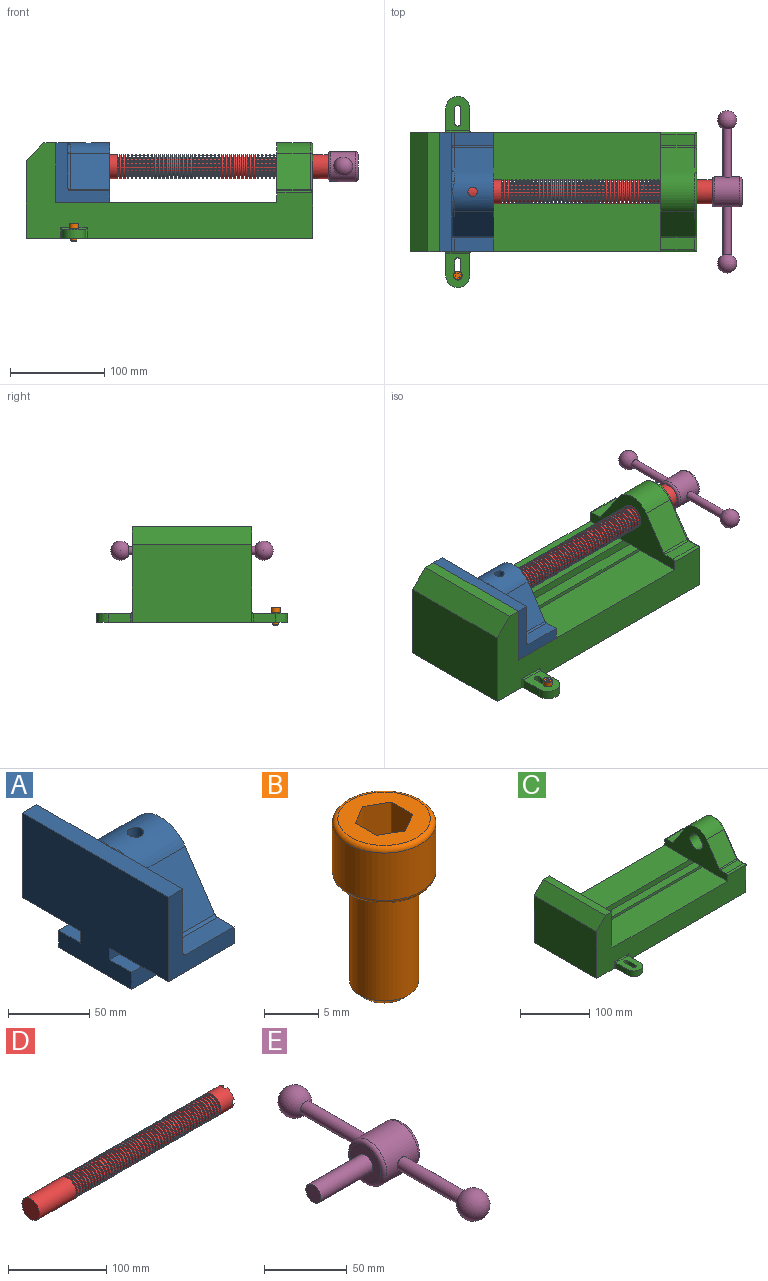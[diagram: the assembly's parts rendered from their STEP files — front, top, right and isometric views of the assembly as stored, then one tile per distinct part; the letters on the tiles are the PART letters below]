
ASSEMBLY  parts=5 mates=5
PART A: 36 faces, bbox 57.2x127x89 mm
  f0: plane 57.15x50.8mm, normal (0,0,-1), area 2903.2mm2, adj f6,f9,f10,f23
  f1: cylinder r=12.7mm len=44.45mm, axis (1,0,0), area 3464.3mm2, adj f6,f15,f16
  f2: plane 41.91x14.52mm, normal (0,0,1), area 608.5mm2, adj f6,f11,f24,f25
  f3: plane 51.86x48.26mm, normal (1,0,0), area 1495.7mm2, adj f8,f10,f31,f33,f35
  f4: plane 51.86x48.26mm, normal (1,0,0), area 1495.7mm2, adj f8,f11,f24,f28,f29
  f5: plane 57.15x50.8mm, normal (0,0,-1), area 2903.2mm2, adj f6,f9,f11,f22
  f6: plane 127x85.09mm, normal (1,0,0), area 5190.6mm2, adj f0,f1,f2,f5,f7,f10,f11,f12
  f7: plane 41.91x14.52mm, normal (0,0,1), area 608.5mm2, adj f6,f10,f30,f31
  f8: plane 127x12.7mm, normal (0,0,1), area 1612.9mm2, adj f3,f4,f9,f10,f11,f26,f34
  f9: plane 127x85.09mm, normal (-1,0,0), area 9096.8mm2, adj f0,f5,f8,f10,f11,f17,f18,f19
  f10: plane 63.5x57.15mm, normal (0,-1,0), area 1372.3mm2, adj f0,f3,f6,f7,f8,f9,f31
  f11: plane 63.5x57.15mm, normal (0,1,0), area 1372.3mm2, adj f2,f4,f5,f6,f8,f9,f24
  f12: plane 41.91x38.43mm, normal (0,-0.83,0.56), area 1939.2mm2, adj f6,f13,f30,f33
  f13: cylinder r=25.4mm len=44.45mm, axis (1,0,0), area 2026.5mm2, adj f6,f12,f14,f16,f26,f28,f34,f35
  f14: plane 41.91x38.43mm, normal (0,0.83,0.56), area 1939.2mm2, adj f6,f13,f25,f29
  f15: plane 25.4x25.4mm, normal (1,0,0), area 506.7mm2, adj f1
  f16: cylinder r=5.08mm len=13.76mm, axis (0,0,1), area 414mm2, adj f1,f13
  f17: plane 57.15x19.05mm, normal (0,0,1), area 1088.7mm2, adj f6,f9,f18,f23
  f18: plane 57.15x12.7mm, normal (0,-1,0), area 725.8mm2, adj f6,f9,f17,f19
  f19: plane 63.5x57.15mm, normal (0,0,-1), area 3629mm2, adj f6,f9,f18,f20
  f20: plane 57.15x12.7mm, normal (0,1,0), area 725.8mm2, adj f6,f9,f19,f21
  f21: plane 57.15x19.05mm, normal (0,0,1), area 1088.7mm2, adj f6,f9,f20,f22
  f22: plane 57.15x8.89mm, normal (0,1,0), area 508.1mm2, adj f5,f6,f9,f21
  f23: plane 57.15x8.89mm, normal (0,-1,0), area 508.1mm2, adj f0,f6,f9,f17
  f24: cylinder r=2.54mm len=14.52mm, axis (0,-1,0), area 57.9mm2, adj f2,f4,f11,f27
  f25: cylinder r=2.54mm len=41.91mm, axis (1,0,0), area 104.3mm2, adj f2,f6,f14,f27
  f26: bspline ~12.24x2.8mm, area 20.9mm2, adj f8,f13,f28
  f27: sphere r=2.54mm, area 6.3mm2, adj f24,f25,f29
  f28: torus R=27.94mm, axis (1,0,0), area 57.8mm2, adj f4,f13,f26,f29
  f29: cylinder r=2.54mm len=39.84mm, axis (0,-0.56,0.83), area 184.6mm2, adj f4,f14,f27,f28
  f30: cylinder r=2.54mm len=41.91mm, axis (1,0,0), area 104.3mm2, adj f6,f7,f12,f32
  f31: cylinder r=2.54mm len=14.52mm, axis (0,-1,0), area 57.9mm2, adj f3,f7,f10,f32
  f32: sphere r=2.54mm, area 6.3mm2, adj f30,f31,f33
  f33: cylinder r=2.54mm len=39.84mm, axis (0,-0.56,-0.83), area 184.6mm2, adj f3,f12,f32,f35
  f34: bspline ~12.24x2.8mm, area 20.9mm2, adj f8,f13,f35
  f35: torus R=27.94mm, axis (1,0,0), area 57.8mm2, adj f3,f13,f33,f34
PART B: 15 faces, bbox 10.3x10.3x19.1 mm
  f0: plane 8.51x8.51mm, normal (0,0,1), area 37.2mm2, adj f5,f6,f7,f8,f9,f10,f14
  f1: cylinder r=3.17mm len=11.94mm, axis (0,0,1), area 238.2mm2, adj f4,f12
  f2: plane 4.83x4.83mm, normal (0,0,-1), area 18.3mm2, adj f12
  f3: cylinder r=4.76mm len=9.53mm, axis (0,0,-1), area 159.6mm2, adj f13,f14
  f4: plane 8.51x8.51mm, normal (0,0,-1), area 25.2mm2, adj f1,f13
  f5: plane 4.83x2.38mm, normal (-0.5,-0.87,0), area 13.3mm2, adj f0,f6,f10,f11
  f6: plane 4.83x2.38mm, normal (0.5,-0.87,0), area 13.3mm2, adj f0,f5,f7,f11
  f7: plane 4.83x2.75mm, normal (1,0,0), area 13.3mm2, adj f0,f6,f8,f11
  f8: plane 4.83x2.38mm, normal (0.5,0.87,0), area 13.3mm2, adj f0,f7,f9,f11
  f9: plane 4.83x2.38mm, normal (-0.5,0.87,0), area 13.3mm2, adj f0,f8,f10,f11
  f10: plane 4.83x2.75mm, normal (-1,0,0), area 13.3mm2, adj f0,f5,f9,f11
  f11: plane 5.5x4.76mm, normal (0,0,1), area 19.6mm2, adj f5,f6,f7,f8,f9,f10
  f12: cone r=3.17mm half-angle=45deg, axis (0,0,1), area 18.9mm2, adj f1,f2
  f13: torus R=4.25mm, axis (0,0,1), area 23mm2, adj f3,f4
  f14: torus R=4.25mm, axis (0,0,1), area 23mm2, adj f0,f3
PART C: 61 faces, bbox 304.8x203.2x103.7 mm
  f0: plane 304.8x101.6mm, normal (0,1,0), area 13520.3mm2, adj f3,f4,f5,f6,f7,f8,f9,f16
  f1: plane 304.8x101.6mm, normal (0,-1,0), area 13520.3mm2, adj f2,f3,f5,f6,f7,f8,f9,f16
  f2: plane 234.95x50.8mm, normal (0,0,1), area 11935.5mm2, adj f1,f5,f16,f26
  f3: plane 127x99.06mm, normal (1,0,0), area 7097.5mm2, adj f0,f1,f9,f14,f17,f18,f19,f20
  f4: plane 234.95x50.8mm, normal (0,0,1), area 11935.5mm2, adj f0,f5,f16,f27
  f5: plane 127x101.6mm, normal (1,0,0), area 9516.1mm2, adj f0,f1,f2,f4,f6,f9,f18,f19
  f6: plane 127x12.7mm, normal (0,0,1), area 1612.9mm2, adj f0,f1,f5,f7
  f7: plane 127x19.05mm, normal (-0.71,0,0.71), area 3421.5mm2, adj f0,f1,f6,f8
  f8: plane 127x82.55mm, normal (-1,0,0), area 10483.8mm2, adj f0,f1,f7,f9
  f9: plane 304.8x203.2mm, normal (0,0,-1), area 33298.3mm2, adj f0,f1,f3,f5,f8,f21,f22,f39
  f10: plane 35.56x11.98mm, normal (0,0,1), area 426mm2, adj f16,f28,f29,f30
  f11: plane 38.43x35.56mm, normal (0,0.83,0.56), area 1645.4mm2, adj f12,f16,f29,f32
  f12: cylinder r=25.4mm len=42.19mm, axis (1,0,0), area 1770.2mm2, adj f11,f13,f16,f33
  f13: plane 38.43x35.56mm, normal (0,-0.83,0.56), area 1645.4mm2, adj f12,f16,f34,f35
  f14: cylinder r=12.7mm len=38.1mm, axis (1,0,0), area 3040.2mm2, adj f3,f16
  f15: plane 35.56x11.98mm, normal (0,0,1), area 426mm2, adj f16,f34,f36,f38
  f16: plane 127x63.5mm, normal (-1,0,0), area 4155.5mm2, adj f0,f1,f2,f4,f10,f11,f12,f13
  f17: plane 38.1x25.4mm, normal (0,0,-1), area 967.7mm2, adj f3,f16,f26,f27
  f18: plane 273.05x19.05mm, normal (0,0,-1), area 5201.6mm2, adj f3,f5,f19,f26
  f19: plane 273.05x12.7mm, normal (0,1,0), area 3467.7mm2, adj f3,f5,f18,f20
  f20: plane 273.05x19.05mm, normal (0,0,1), area 5201.6mm2, adj f3,f5,f19,f21
  f21: plane 273.05x16.51mm, normal (0,1,0), area 4508.1mm2, adj f3,f5,f9,f20
  f22: plane 273.05x16.51mm, normal (0,-1,0), area 4508.1mm2, adj f3,f5,f9,f23
  f23: plane 273.05x19.05mm, normal (0,0,1), area 5201.6mm2, adj f3,f5,f22,f24
  f24: plane 273.05x12.7mm, normal (0,-1,0), area 3467.7mm2, adj f3,f5,f23,f25
  f25: plane 273.05x19.05mm, normal (0,0,-1), area 5201.6mm2, adj f3,f5,f24,f27
  f26: plane 273.05x8.89mm, normal (0,1,0), area 2427.4mm2, adj f2,f3,f5,f17,f18
  f27: plane 273.05x8.89mm, normal (0,-1,0), area 2427.4mm2, adj f3,f4,f5,f17,f25
  f28: cylinder r=2.54mm len=38.1mm, axis (1,0,0), area 148.3mm2, adj f0,f10,f16,f30
  f29: cylinder r=2.54mm len=35.56mm, axis (-1,0,0), area 88.5mm2, adj f10,f11,f16,f31
  f30: cylinder r=2.54mm len=14.52mm, axis (0,1,0), area 54.3mm2, adj f3,f10,f28,f31
  f31: torus R=5.08mm, axis (-1,0,0), area 13.5mm2, adj f3,f29,f30,f32
  f32: cylinder r=2.54mm len=39.84mm, axis (0,0.56,-0.83), area 184.6mm2, adj f3,f11,f31,f33
  f33: torus R=22.86mm, axis (-1,0,0), area 191.4mm2, adj f3,f12,f32,f35
  f34: cylinder r=2.54mm len=35.56mm, axis (-1,0,0), area 88.5mm2, adj f13,f15,f16,f37
  f35: cylinder r=2.54mm len=39.84mm, axis (0,0.56,0.83), area 184.6mm2, adj f3,f13,f33,f37
  f36: cylinder r=2.54mm len=38.1mm, axis (-1,0,0), area 148.3mm2, adj f1,f15,f16,f38
  f37: torus R=5.08mm, axis (-1,0,0), area 13.5mm2, adj f3,f34,f35,f38
  f38: cylinder r=2.54mm len=14.52mm, axis (0,1,0), area 54.3mm2, adj f3,f15,f36,f37
  f39: plane 23.88x9.53mm, normal (-1,0,0), area 227.4mm2, adj f9,f45,f46,f60
  f40: plane 23.88x9.53mm, normal (1,0,0), area 227.4mm2, adj f9,f45,f46,f58
  f41: cylinder r=3.3mm len=9.53mm, axis (0,0,-1), area 98.8mm2, adj f9,f42,f44,f46
  f42: plane 15.62x9.53mm, normal (-1,0,0), area 148.8mm2, adj f9,f41,f43,f46
  f43: cylinder r=3.3mm len=9.53mm, axis (0,0,-1), area 98.8mm2, adj f9,f42,f44,f46
  f44: plane 15.62x9.53mm, normal (1,0,0), area 148.8mm2, adj f9,f41,f43,f46
  f45: cylinder r=12.7mm len=25.4mm, axis (0,0,-1), area 380mm2, adj f9,f39,f40,f46
  f46: plane 36.58x25.4mm, normal (0,0,1), area 722.4mm2, adj f39,f40,f41,f42,f43,f44,f45,f59
  f47: plane 23.88x9.53mm, normal (-1,0,0), area 227.4mm2, adj f9,f53,f54,f56
  f48: plane 23.88x9.53mm, normal (1,0,0), area 227.4mm2, adj f9,f53,f54,f55
  f49: cylinder r=3.3mm len=9.53mm, axis (0,0,-1), area 98.8mm2, adj f9,f50,f52,f54
  f50: plane 15.62x9.53mm, normal (-1,0,0), area 148.8mm2, adj f9,f49,f51,f54
  f51: cylinder r=3.3mm len=9.53mm, axis (0,0,-1), area 98.8mm2, adj f9,f50,f52,f54
  f52: plane 15.62x9.53mm, normal (1,0,0), area 148.8mm2, adj f9,f49,f51,f54
  f53: cylinder r=12.7mm len=25.4mm, axis (0,0,-1), area 380mm2, adj f9,f47,f48,f54
  f54: plane 36.58x25.4mm, normal (0,0,1), area 722.4mm2, adj f47,f48,f49,f50,f51,f52,f53,f57
  f55: cylinder r=1.52mm len=11.05mm, axis (0,0,-1), area 24.1mm2, adj f0,f9,f48,f57
  f56: cylinder r=1.52mm len=11.05mm, axis (0,0,1), area 24.1mm2, adj f0,f9,f47,f57
  f57: cylinder r=1.52mm len=28.45mm, axis (1,0,0), area 63.5mm2, adj f0,f54,f55,f56
  f58: cylinder r=1.52mm len=11.05mm, axis (0,0,1), area 24.1mm2, adj f1,f9,f40,f59
  f59: cylinder r=1.52mm len=28.45mm, axis (-1,0,0), area 63.5mm2, adj f1,f46,f58,f60
  f60: cylinder r=1.52mm len=11.05mm, axis (0,0,-1), area 24.1mm2, adj f1,f9,f39,f59
PART D: 220 faces, bbox 279.4x25.4x25.4 mm
  f0: cylinder r=12.7mm len=25.4mm, axis (-1,0,0), area 1468.2mm2, adj f1,f2,f3,f5,f7,f208,f209,f210
  f1: plane 9.9x9.9mm, normal (1,0,0), area 62.3mm2, adj f0,f4,f213,f216
  f2: plane 9.9x9.9mm, normal (1,0,0), area 62.3mm2, adj f0,f4,f210,f218
  f3: plane 9.9x9.9mm, normal (1,0,0), area 62.3mm2, adj f0,f4,f209,f212
  f4: cylinder r=6.35mm len=25.4mm, axis (1,0,0), area 960.3mm2, adj f1,f2,f3,f5,f6,f208,f209,f210
  f5: plane 9.9x9.9mm, normal (1,0,0), area 62.3mm2, adj f0,f4,f215,f217
  f6: plane 12.7x12.7mm, normal (1,0,0), area 126.7mm2, adj f4
  f7: cone r=12.7mm half-angle=76deg, axis (1,0,0), area 188mm2, adj f0,f9
  f8: cone r=10.16mm half-angle=76deg, axis (-1,0,0), area 188mm2, adj f9,f10
  f9: cylinder r=10.16mm len=20.32mm, axis (1,0,0), area 81.1mm2, adj f7,f8
  f10: cylinder r=12.7mm len=25.4mm, axis (-1,0,0), area 131.7mm2, adj f8,f11
  f11: cone r=12.7mm half-angle=76deg, axis (1,0,0), area 188mm2, adj f10,f13
  f12: cone r=10.16mm half-angle=76deg, axis (-1,0,0), area 188mm2, adj f13,f14
  f13: cylinder r=10.16mm len=20.32mm, axis (1,0,0), area 81.1mm2, adj f11,f12
  f14: cylinder r=12.7mm len=25.4mm, axis (-1,0,0), area 131.7mm2, adj f12,f15
  f15: cone r=12.7mm half-angle=76deg, axis (1,0,0), area 188mm2, adj f14,f17
  f16: cone r=10.16mm half-angle=76deg, axis (-1,0,0), area 188mm2, adj f17,f18
  f17: cylinder r=10.16mm len=20.32mm, axis (1,0,0), area 81.1mm2, adj f15,f16
  f18: cylinder r=12.7mm len=25.4mm, axis (-1,0,0), area 131.7mm2, adj f16,f19
  f19: cone r=12.7mm half-angle=76deg, axis (1,0,0), area 188mm2, adj f18,f21
  f20: cone r=10.16mm half-angle=76deg, axis (-1,0,0), area 188mm2, adj f21,f22
  f21: cylinder r=10.16mm len=20.32mm, axis (1,0,0), area 81.1mm2, adj f19,f20
  f22: cylinder r=12.7mm len=25.4mm, axis (-1,0,0), area 131.7mm2, adj f20,f23
  f23: cone r=12.7mm half-angle=76deg, axis (1,0,0), area 188mm2, adj f22,f25
  f24: cone r=10.16mm half-angle=76deg, axis (-1,0,0), area 188mm2, adj f25,f26
  f25: cylinder r=10.16mm len=20.32mm, axis (1,0,0), area 81.1mm2, adj f23,f24
  f26: cylinder r=12.7mm len=25.4mm, axis (-1,0,0), area 131.7mm2, adj f24,f27
  f27: cone r=12.7mm half-angle=76deg, axis (1,0,0), area 188mm2, adj f26,f29
  f28: cone r=10.16mm half-angle=76deg, axis (-1,0,0), area 188mm2, adj f29,f30
  f29: cylinder r=10.16mm len=20.32mm, axis (1,0,0), area 81.1mm2, adj f27,f28
  f30: cylinder r=12.7mm len=25.4mm, axis (-1,0,0), area 131.7mm2, adj f28,f31
  f31: cone r=12.7mm half-angle=76deg, axis (1,0,0), area 188mm2, adj f30,f33
  f32: cone r=10.16mm half-angle=76deg, axis (-1,0,0), area 188mm2, adj f33,f34
  f33: cylinder r=10.16mm len=20.32mm, axis (1,0,0), area 81.1mm2, adj f31,f32
  f34: cylinder r=12.7mm len=25.4mm, axis (-1,0,0), area 131.7mm2, adj f32,f35
  f35: cone r=12.7mm half-angle=76deg, axis (1,0,0), area 188mm2, adj f34,f37
  f36: cone r=10.16mm half-angle=76deg, axis (-1,0,0), area 188mm2, adj f37,f38
  f37: cylinder r=10.16mm len=20.32mm, axis (1,0,0), area 81.1mm2, adj f35,f36
  f38: cylinder r=12.7mm len=25.4mm, axis (-1,0,0), area 131.7mm2, adj f36,f39
  f39: cone r=12.7mm half-angle=76deg, axis (1,0,0), area 188mm2, adj f38,f41
  f40: cone r=10.16mm half-angle=76deg, axis (-1,0,0), area 188mm2, adj f41,f42
  f41: cylinder r=10.16mm len=20.32mm, axis (1,0,0), area 81.1mm2, adj f39,f40
  f42: cylinder r=12.7mm len=25.4mm, axis (-1,0,0), area 131.7mm2, adj f40,f43
  f43: cone r=12.7mm half-angle=76deg, axis (1,0,0), area 188mm2, adj f42,f45
  f44: cone r=10.16mm half-angle=76deg, axis (-1,0,0), area 188mm2, adj f45,f46
  f45: cylinder r=10.16mm len=20.32mm, axis (1,0,0), area 81.1mm2, adj f43,f44
  f46: cylinder r=12.7mm len=25.4mm, axis (-1,0,0), area 131.7mm2, adj f44,f47
  f47: cone r=12.7mm half-angle=76deg, axis (1,0,0), area 188mm2, adj f46,f49
  f48: cone r=10.16mm half-angle=76deg, axis (-1,0,0), area 188mm2, adj f49,f50
  f49: cylinder r=10.16mm len=20.32mm, axis (1,0,0), area 81.1mm2, adj f47,f48
  f50: cylinder r=12.7mm len=25.4mm, axis (-1,0,0), area 131.7mm2, adj f48,f51
  f51: cone r=12.7mm half-angle=76deg, axis (1,0,0), area 188mm2, adj f50,f53
  f52: cone r=10.16mm half-angle=76deg, axis (-1,0,0), area 188mm2, adj f53,f54
  f53: cylinder r=10.16mm len=20.32mm, axis (1,0,0), area 81.1mm2, adj f51,f52
  f54: cylinder r=12.7mm len=25.4mm, axis (-1,0,0), area 131.7mm2, adj f52,f55
  f55: cone r=12.7mm half-angle=76deg, axis (1,0,0), area 188mm2, adj f54,f57
  f56: cone r=10.16mm half-angle=76deg, axis (-1,0,0), area 188mm2, adj f57,f58
  f57: cylinder r=10.16mm len=20.32mm, axis (1,0,0), area 81.1mm2, adj f55,f56
  f58: cylinder r=12.7mm len=25.4mm, axis (-1,0,0), area 131.7mm2, adj f56,f59
  f59: cone r=12.7mm half-angle=76deg, axis (1,0,0), area 188mm2, adj f58,f61
  f60: cone r=10.16mm half-angle=76deg, axis (-1,0,0), area 188mm2, adj f61,f62
  f61: cylinder r=10.16mm len=20.32mm, axis (1,0,0), area 81.1mm2, adj f59,f60
  f62: cylinder r=12.7mm len=25.4mm, axis (-1,0,0), area 131.7mm2, adj f60,f63
  f63: cone r=12.7mm half-angle=76deg, axis (1,0,0), area 188mm2, adj f62,f65
  f64: cone r=10.16mm half-angle=76deg, axis (-1,0,0), area 188mm2, adj f65,f66
  f65: cylinder r=10.16mm len=20.32mm, axis (1,0,0), area 81.1mm2, adj f63,f64
  f66: cylinder r=12.7mm len=25.4mm, axis (-1,0,0), area 131.7mm2, adj f64,f67
  f67: cone r=12.7mm half-angle=76deg, axis (1,0,0), area 188mm2, adj f66,f69
  f68: cone r=10.16mm half-angle=76deg, axis (-1,0,0), area 188mm2, adj f69,f70
  f69: cylinder r=10.16mm len=20.32mm, axis (1,0,0), area 81.1mm2, adj f67,f68
  f70: cylinder r=12.7mm len=25.4mm, axis (-1,0,0), area 131.7mm2, adj f68,f71
  f71: cone r=12.7mm half-angle=76deg, axis (1,0,0), area 188mm2, adj f70,f73
  f72: cone r=10.16mm half-angle=76deg, axis (-1,0,0), area 188mm2, adj f73,f74
  f73: cylinder r=10.16mm len=20.32mm, axis (1,0,0), area 81.1mm2, adj f71,f72
  f74: cylinder r=12.7mm len=25.4mm, axis (-1,0,0), area 131.7mm2, adj f72,f75
  f75: cone r=12.7mm half-angle=76deg, axis (1,0,0), area 188mm2, adj f74,f77
  f76: cone r=10.16mm half-angle=76deg, axis (-1,0,0), area 188mm2, adj f77,f78
  f77: cylinder r=10.16mm len=20.32mm, axis (1,0,0), area 81.1mm2, adj f75,f76
  f78: cylinder r=12.7mm len=25.4mm, axis (-1,0,0), area 131.7mm2, adj f76,f79
  f79: cone r=12.7mm half-angle=76deg, axis (1,0,0), area 188mm2, adj f78,f81
  f80: cone r=10.16mm half-angle=76deg, axis (-1,0,0), area 188mm2, adj f81,f82
  f81: cylinder r=10.16mm len=20.32mm, axis (1,0,0), area 81.1mm2, adj f79,f80
  f82: cylinder r=12.7mm len=25.4mm, axis (-1,0,0), area 131.7mm2, adj f80,f83
  f83: cone r=12.7mm half-angle=76deg, axis (1,0,0), area 188mm2, adj f82,f85
  f84: cone r=10.16mm half-angle=76deg, axis (-1,0,0), area 188mm2, adj f85,f86
  f85: cylinder r=10.16mm len=20.32mm, axis (1,0,0), area 81.1mm2, adj f83,f84
  f86: cylinder r=12.7mm len=25.4mm, axis (-1,0,0), area 131.7mm2, adj f84,f87
  f87: cone r=12.7mm half-angle=76deg, axis (1,0,0), area 188mm2, adj f86,f89
  f88: cone r=10.16mm half-angle=76deg, axis (-1,0,0), area 188mm2, adj f89,f90
  f89: cylinder r=10.16mm len=20.32mm, axis (1,0,0), area 81.1mm2, adj f87,f88
  f90: cylinder r=12.7mm len=25.4mm, axis (-1,0,0), area 131.7mm2, adj f88,f91
  f91: cone r=12.7mm half-angle=76deg, axis (1,0,0), area 188mm2, adj f90,f93
  f92: cone r=10.16mm half-angle=76deg, axis (-1,0,0), area 188mm2, adj f93,f94
  f93: cylinder r=10.16mm len=20.32mm, axis (1,0,0), area 81.1mm2, adj f91,f92
  f94: cylinder r=12.7mm len=25.4mm, axis (-1,0,0), area 131.7mm2, adj f92,f95
  f95: cone r=12.7mm half-angle=76deg, axis (1,0,0), area 188mm2, adj f94,f97
  f96: cone r=10.16mm half-angle=76deg, axis (-1,0,0), area 188mm2, adj f97,f98
  f97: cylinder r=10.16mm len=20.32mm, axis (1,0,0), area 81.1mm2, adj f95,f96
  f98: cylinder r=12.7mm len=25.4mm, axis (-1,0,0), area 131.7mm2, adj f96,f99
  f99: cone r=12.7mm half-angle=76deg, axis (1,0,0), area 188mm2, adj f98,f101
  f100: cone r=10.16mm half-angle=76deg, axis (-1,0,0), area 188mm2, adj f101,f102
  f101: cylinder r=10.16mm len=20.32mm, axis (1,0,0), area 81.1mm2, adj f99,f100
  f102: cylinder r=12.7mm len=25.4mm, axis (-1,0,0), area 131.7mm2, adj f100,f103
  f103: cone r=12.7mm half-angle=76deg, axis (1,0,0), area 188mm2, adj f102,f105
  f104: cone r=10.16mm half-angle=76deg, axis (-1,0,0), area 188mm2, adj f105,f106
  f105: cylinder r=10.16mm len=20.32mm, axis (1,0,0), area 81.1mm2, adj f103,f104
  f106: cylinder r=12.7mm len=25.4mm, axis (-1,0,0), area 131.7mm2, adj f104,f107
  f107: cone r=12.7mm half-angle=76deg, axis (1,0,0), area 188mm2, adj f106,f109
  f108: cone r=10.16mm half-angle=76deg, axis (-1,0,0), area 188mm2, adj f109,f110
  f109: cylinder r=10.16mm len=20.32mm, axis (1,0,0), area 81.1mm2, adj f107,f108
  f110: cylinder r=12.7mm len=25.4mm, axis (-1,0,0), area 131.7mm2, adj f108,f111
  f111: cone r=12.7mm half-angle=76deg, axis (1,0,0), area 188mm2, adj f110,f113
  f112: cone r=10.16mm half-angle=76deg, axis (-1,0,0), area 188mm2, adj f113,f114
  f113: cylinder r=10.16mm len=20.32mm, axis (1,0,0), area 81.1mm2, adj f111,f112
  f114: cylinder r=12.7mm len=25.4mm, axis (-1,0,0), area 131.7mm2, adj f112,f115
  f115: cone r=12.7mm half-angle=76deg, axis (1,0,0), area 188mm2, adj f114,f117
  f116: cone r=10.16mm half-angle=76deg, axis (-1,0,0), area 188mm2, adj f117,f118
  f117: cylinder r=10.16mm len=20.32mm, axis (1,0,0), area 81.1mm2, adj f115,f116
  f118: cylinder r=12.7mm len=25.4mm, axis (-1,0,0), area 131.7mm2, adj f116,f119
  f119: cone r=12.7mm half-angle=76deg, axis (1,0,0), area 188mm2, adj f118,f121
  f120: cone r=10.16mm half-angle=76deg, axis (-1,0,0), area 188mm2, adj f121,f122
  f121: cylinder r=10.16mm len=20.32mm, axis (1,0,0), area 81.1mm2, adj f119,f120
  f122: cylinder r=12.7mm len=25.4mm, axis (-1,0,0), area 131.7mm2, adj f120,f123
  f123: cone r=12.7mm half-angle=76deg, axis (1,0,0), area 188mm2, adj f122,f125
  f124: cone r=10.16mm half-angle=76deg, axis (-1,0,0), area 188mm2, adj f125,f126
  f125: cylinder r=10.16mm len=20.32mm, axis (1,0,0), area 81.1mm2, adj f123,f124
  f126: cylinder r=12.7mm len=25.4mm, axis (-1,0,0), area 131.7mm2, adj f124,f127
  f127: cone r=12.7mm half-angle=76deg, axis (1,0,0), area 188mm2, adj f126,f129
  f128: cone r=10.16mm half-angle=76deg, axis (-1,0,0), area 188mm2, adj f129,f130
  f129: cylinder r=10.16mm len=20.32mm, axis (1,0,0), area 81.1mm2, adj f127,f128
  f130: cylinder r=12.7mm len=25.4mm, axis (-1,0,0), area 131.7mm2, adj f128,f131
  f131: cone r=12.7mm half-angle=76deg, axis (1,0,0), area 188mm2, adj f130,f133
  f132: cone r=10.16mm half-angle=76deg, axis (-1,0,0), area 188mm2, adj f133,f134
  f133: cylinder r=10.16mm len=20.32mm, axis (1,0,0), area 81.1mm2, adj f131,f132
  f134: cylinder r=12.7mm len=25.4mm, axis (-1,0,0), area 131.7mm2, adj f132,f135
  f135: cone r=12.7mm half-angle=76deg, axis (1,0,0), area 188mm2, adj f134,f137
  f136: cone r=10.16mm half-angle=76deg, axis (-1,0,0), area 188mm2, adj f137,f138
  f137: cylinder r=10.16mm len=20.32mm, axis (1,0,0), area 81.1mm2, adj f135,f136
  f138: cylinder r=12.7mm len=25.4mm, axis (-1,0,0), area 131.7mm2, adj f136,f139
  f139: cone r=12.7mm half-angle=76deg, axis (1,0,0), area 188mm2, adj f138,f141
  f140: cone r=10.16mm half-angle=76deg, axis (-1,0,0), area 188mm2, adj f141,f142
  f141: cylinder r=10.16mm len=20.32mm, axis (1,0,0), area 81.1mm2, adj f139,f140
  f142: cylinder r=12.7mm len=25.4mm, axis (-1,0,0), area 131.7mm2, adj f140,f143
  f143: cone r=12.7mm half-angle=76deg, axis (1,0,0), area 188mm2, adj f142,f145
  f144: cone r=10.16mm half-angle=76deg, axis (-1,0,0), area 188mm2, adj f145,f146
  f145: cylinder r=10.16mm len=20.32mm, axis (1,0,0), area 81.1mm2, adj f143,f144
  f146: cylinder r=12.7mm len=25.4mm, axis (-1,0,0), area 131.7mm2, adj f144,f147
  f147: cone r=12.7mm half-angle=76deg, axis (1,0,0), area 188mm2, adj f146,f149
  f148: cone r=10.16mm half-angle=76deg, axis (-1,0,0), area 188mm2, adj f149,f150
  f149: cylinder r=10.16mm len=20.32mm, axis (1,0,0), area 81.1mm2, adj f147,f148
  f150: cylinder r=12.7mm len=25.4mm, axis (-1,0,0), area 131.7mm2, adj f148,f151
  f151: cone r=12.7mm half-angle=76deg, axis (1,0,0), area 188mm2, adj f150,f153
  f152: cone r=10.16mm half-angle=76deg, axis (-1,0,0), area 188mm2, adj f153,f154
  f153: cylinder r=10.16mm len=20.32mm, axis (1,0,0), area 81.1mm2, adj f151,f152
  f154: cylinder r=12.7mm len=25.4mm, axis (-1,0,0), area 131.7mm2, adj f152,f155
  f155: cone r=12.7mm half-angle=76deg, axis (1,0,0), area 188mm2, adj f154,f157
  f156: cone r=10.16mm half-angle=76deg, axis (-1,0,0), area 188mm2, adj f157,f158
  f157: cylinder r=10.16mm len=20.32mm, axis (1,0,0), area 81.1mm2, adj f155,f156
  f158: cylinder r=12.7mm len=25.4mm, axis (-1,0,0), area 131.7mm2, adj f156,f159
  f159: cone r=12.7mm half-angle=76deg, axis (1,0,0), area 188mm2, adj f158,f161
  f160: cone r=10.16mm half-angle=76deg, axis (-1,0,0), area 188mm2, adj f161,f162
  f161: cylinder r=10.16mm len=20.32mm, axis (1,0,0), area 81.1mm2, adj f159,f160
  f162: cylinder r=12.7mm len=25.4mm, axis (-1,0,0), area 131.7mm2, adj f160,f163
  f163: cone r=12.7mm half-angle=76deg, axis (1,0,0), area 188mm2, adj f162,f165
  f164: cone r=10.16mm half-angle=76deg, axis (-1,0,0), area 188mm2, adj f165,f166
  f165: cylinder r=10.16mm len=20.32mm, axis (1,0,0), area 81.1mm2, adj f163,f164
  f166: cylinder r=12.7mm len=25.4mm, axis (-1,0,0), area 131.7mm2, adj f164,f167
  f167: cone r=12.7mm half-angle=76deg, axis (1,0,0), area 188mm2, adj f166,f169
  f168: cone r=10.16mm half-angle=76deg, axis (-1,0,0), area 188mm2, adj f169,f170
  f169: cylinder r=10.16mm len=20.32mm, axis (1,0,0), area 81.1mm2, adj f167,f168
  f170: cylinder r=12.7mm len=25.4mm, axis (-1,0,0), area 131.7mm2, adj f168,f171
  f171: cone r=12.7mm half-angle=76deg, axis (1,0,0), area 188mm2, adj f170,f173
  f172: cone r=10.16mm half-angle=76deg, axis (-1,0,0), area 188mm2, adj f173,f174
  f173: cylinder r=10.16mm len=20.32mm, axis (1,0,0), area 81.1mm2, adj f171,f172
  f174: cylinder r=12.7mm len=25.4mm, axis (-1,0,0), area 131.7mm2, adj f172,f175
  f175: cone r=12.7mm half-angle=76deg, axis (1,0,0), area 188mm2, adj f174,f177
  f176: cone r=10.16mm half-angle=76deg, axis (-1,0,0), area 188mm2, adj f177,f178
  f177: cylinder r=10.16mm len=20.32mm, axis (1,0,0), area 81.1mm2, adj f175,f176
  f178: cylinder r=12.7mm len=25.4mm, axis (-1,0,0), area 131.7mm2, adj f176,f179
  f179: cone r=12.7mm half-angle=76deg, axis (1,0,0), area 188mm2, adj f178,f181
  f180: cone r=10.16mm half-angle=76deg, axis (-1,0,0), area 188mm2, adj f181,f182
  f181: cylinder r=10.16mm len=20.32mm, axis (1,0,0), area 81.1mm2, adj f179,f180
  f182: cylinder r=12.7mm len=25.4mm, axis (-1,0,0), area 131.7mm2, adj f180,f183
  f183: cone r=12.7mm half-angle=76deg, axis (1,0,0), area 188mm2, adj f182,f185
  f184: cone r=10.16mm half-angle=76deg, axis (-1,0,0), area 188mm2, adj f185,f186
  f185: cylinder r=10.16mm len=20.32mm, axis (1,0,0), area 81.1mm2, adj f183,f184
  f186: cylinder r=12.7mm len=25.4mm, axis (-1,0,0), area 131.7mm2, adj f184,f187
  f187: cone r=12.7mm half-angle=76deg, axis (1,0,0), area 188mm2, adj f186,f189
  f188: cone r=10.16mm half-angle=76deg, axis (-1,0,0), area 188mm2, adj f189,f190
  f189: cylinder r=10.16mm len=20.32mm, axis (1,0,0), area 81.1mm2, adj f187,f188
  f190: cylinder r=12.7mm len=25.4mm, axis (-1,0,0), area 131.7mm2, adj f188,f191
  f191: cone r=12.7mm half-angle=76deg, axis (1,0,0), area 188mm2, adj f190,f193
  f192: cone r=10.16mm half-angle=76deg, axis (-1,0,0), area 188mm2, adj f193,f194
  f193: cylinder r=10.16mm len=20.32mm, axis (1,0,0), area 81.1mm2, adj f191,f192
  f194: cylinder r=12.7mm len=25.4mm, axis (-1,0,0), area 131.7mm2, adj f192,f195
  f195: cone r=12.7mm half-angle=76deg, axis (1,0,0), area 188mm2, adj f194,f197
  f196: cone r=10.16mm half-angle=76deg, axis (-1,0,0), area 188mm2, adj f197,f198
  f197: cylinder r=10.16mm len=20.32mm, axis (1,0,0), area 81.1mm2, adj f195,f196
  f198: cylinder r=12.7mm len=25.4mm, axis (-1,0,0), area 131.7mm2, adj f196,f199
  f199: cone r=12.7mm half-angle=76deg, axis (1,0,0), area 188mm2, adj f198,f201
  f200: cone r=10.16mm half-angle=76deg, axis (-1,0,0), area 188mm2, adj f201,f202
  f201: cylinder r=10.16mm len=20.32mm, axis (1,0,0), area 81.1mm2, adj f199,f200
  f202: cylinder r=12.7mm len=25.4mm, axis (-1,0,0), area 131.7mm2, adj f200,f203
  f203: cone r=12.7mm half-angle=76deg, axis (1,0,0), area 188mm2, adj f202,f205
  f204: cone r=10.16mm half-angle=76deg, axis (-1,0,0), area 188mm2, adj f205,f207
  f205: cylinder r=10.16mm len=20.32mm, axis (1,0,0), area 81.1mm2, adj f203,f204
  f206: plane 25.4x25.4mm, normal (-1,0,0), area 506.7mm2, adj f207
  f207: cylinder r=12.7mm len=52.45mm, axis (-1,0,0), area 4185.4mm2, adj f204,f206
  f208: plane 6.88x5.08mm, normal (1,0,0), area 32.7mm2, adj f0,f4,f209,f210
  f209: plane 6.62x2.54mm, normal (0,-1,0), area 16.8mm2, adj f0,f3,f4,f208
  f210: plane 6.62x2.54mm, normal (0,1,0), area 16.8mm2, adj f0,f2,f4,f208
  f211: plane 6.88x5.08mm, normal (1,0,0), area 32.7mm2, adj f0,f4,f212,f213
  f212: plane 6.62x2.54mm, normal (0,0,1), area 16.8mm2, adj f0,f3,f4,f211
  f213: plane 6.62x2.54mm, normal (0,0,-1), area 16.8mm2, adj f0,f1,f4,f211
  f214: plane 6.88x5.08mm, normal (1,0,0), area 32.7mm2, adj f0,f4,f215,f216
  f215: plane 6.62x2.54mm, normal (0,1,0), area 16.8mm2, adj f0,f4,f5,f214
  f216: plane 6.62x2.54mm, normal (0,-1,0), area 16.8mm2, adj f0,f1,f4,f214
  f217: plane 6.62x2.54mm, normal (0,0,-1), area 16.8mm2, adj f0,f4,f5,f219
  f218: plane 6.62x2.54mm, normal (0,0,1), area 16.8mm2, adj f0,f2,f4,f219
  f219: plane 6.88x5.08mm, normal (1,0,0), area 32.7mm2, adj f0,f4,f217,f218
PART E: 11 faces, bbox 76.2x172.7x34.4 mm
  f0: sphere r=10.16mm, area 1231.8mm2, adj f1
  f1: cylinder r=4.45mm len=51.82mm, axis (0,1,0), area 1438.5mm2, adj f0,f4
  f2: sphere r=10.16mm, area 1231.8mm2, adj f3
  f3: cylinder r=4.45mm len=51.82mm, axis (0,1,0), area 1438.5mm2, adj f2,f4
  f4: cylinder r=15.88mm len=31.75mm, axis (-1,0,0), area 2534.7mm2, adj f1,f3,f9,f10
  f5: cylinder r=6.35mm len=44.45mm, axis (-1,0,0), area 1773.5mm2, adj f6,f8
  f6: plane 12.7x12.7mm, normal (-1,0,0), area 126.7mm2, adj f5
  f7: plane 26.67x26.67mm, normal (1,0,0), area 558.6mm2, adj f10
  f8: plane 26.67x26.67mm, normal (-1,0,0), area 432mm2, adj f5,f9
  f9: torus R=13.33mm, axis (1,0,0), area 374.8mm2, adj f4,f8
  f10: torus R=13.33mm, axis (1,0,0), area 374.8mm2, adj f4,f7
PLACE A at identity
PLACE B rot(axis=(0,0,-1),71.6deg) t=(-254,-88.9,9.52)mm
PLACE C at identity fixed
PLACE D rot(axis=(1,0,0),180deg) t=(0,0,152.4)mm
PLACE E rot(axis=(1,0,0),180deg) t=(-21.59,0,152.4)mm
MATE fastened D.f4 <-> E.f5  axis (1,0,0) through (16.51,0,76.2)mm
MATE planar A.f0 <-> C.f2  axis (0,0,-1) through (-244.48,-38.1,38.1)mm
MATE pin_slot B.f1 <-> C.f41  axis (0,0,1) through (-254,-88.9,9.52)mm
MATE revolute D.f7 <-> A.f28  axis (-1,0,0) through (-260.35,0,76.2)mm
MATE cylindrical C.f12 <-> D.f7  axis (-1,0,0) through (-38.1,0,76.2)mm
